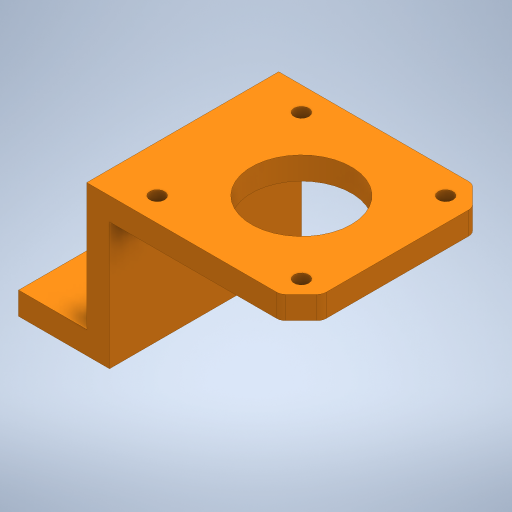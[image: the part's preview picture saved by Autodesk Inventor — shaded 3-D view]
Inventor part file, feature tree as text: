
AUTODESK INVENTOR PART (.ipt)
format: ipt  version: 2023 (Build 270158000, 158)  size: 302,592 bytes
history: native  units: mm
features: extrude x6, sketch x6, other x3, reference x2, plane x1
ambient origin geometry x8: Origin, YZ Plane, XZ Plane, XY Plane, X Axis, Y Axis, Z Axis, Center Point
bodies: Solid1 (feature_tree)
feature tree (18):
  extrude  "Extrusion1"  Depth=5.0mm TaperAngle=0.0deg
  extrude  "Extrusion2"  Depth=33.0mm
  extrude  "Extrusion3"  Depth=15.0mm TaperAngle=0.0deg
  extrude  "Extrusion4"  Depth=10.0mm
  extrude  "Extrusion5"  Depth=10.0mm
  plane  "Work Plane1"
  extrude  "Extrusion6"  Depth=10.0mm
  sketch  "Sketch1"  dims[d0=5.0mm d1=0.0mm d2=5.0mm d3=0.0mm]
  reference  "Reference1"
  reference  "Reference2"
  sketch  "Sketch2"  dims[d4=5.0mm d5=0.0mm d6=33.0mm]
  sketch  "Sketch3"  dims[d7=5.0mm d8=15.0mm d9=0.0mm]
  sketch  "Sketch4"  dims[d10=10.0mm d11=10.0mm]
  sketch  "Sketch5"  dims[d12=10.0mm d13=10.0mm]
  sketch  "Sketch6"  dims[d14=4.5mm d15=4.5mm d16=0.0mm d17=0.0mm d18=10.0mm d19=0.0mm]
  other  "<userpath>\OneDrive\ClawdDrive\Objet3D\3DPrinter\inventor\3DPrinterBeltCoreXY.iam"
  other  "3DPrinterBeltCoreXY.iam"
  other  "E3D Stepper Motor:4"
